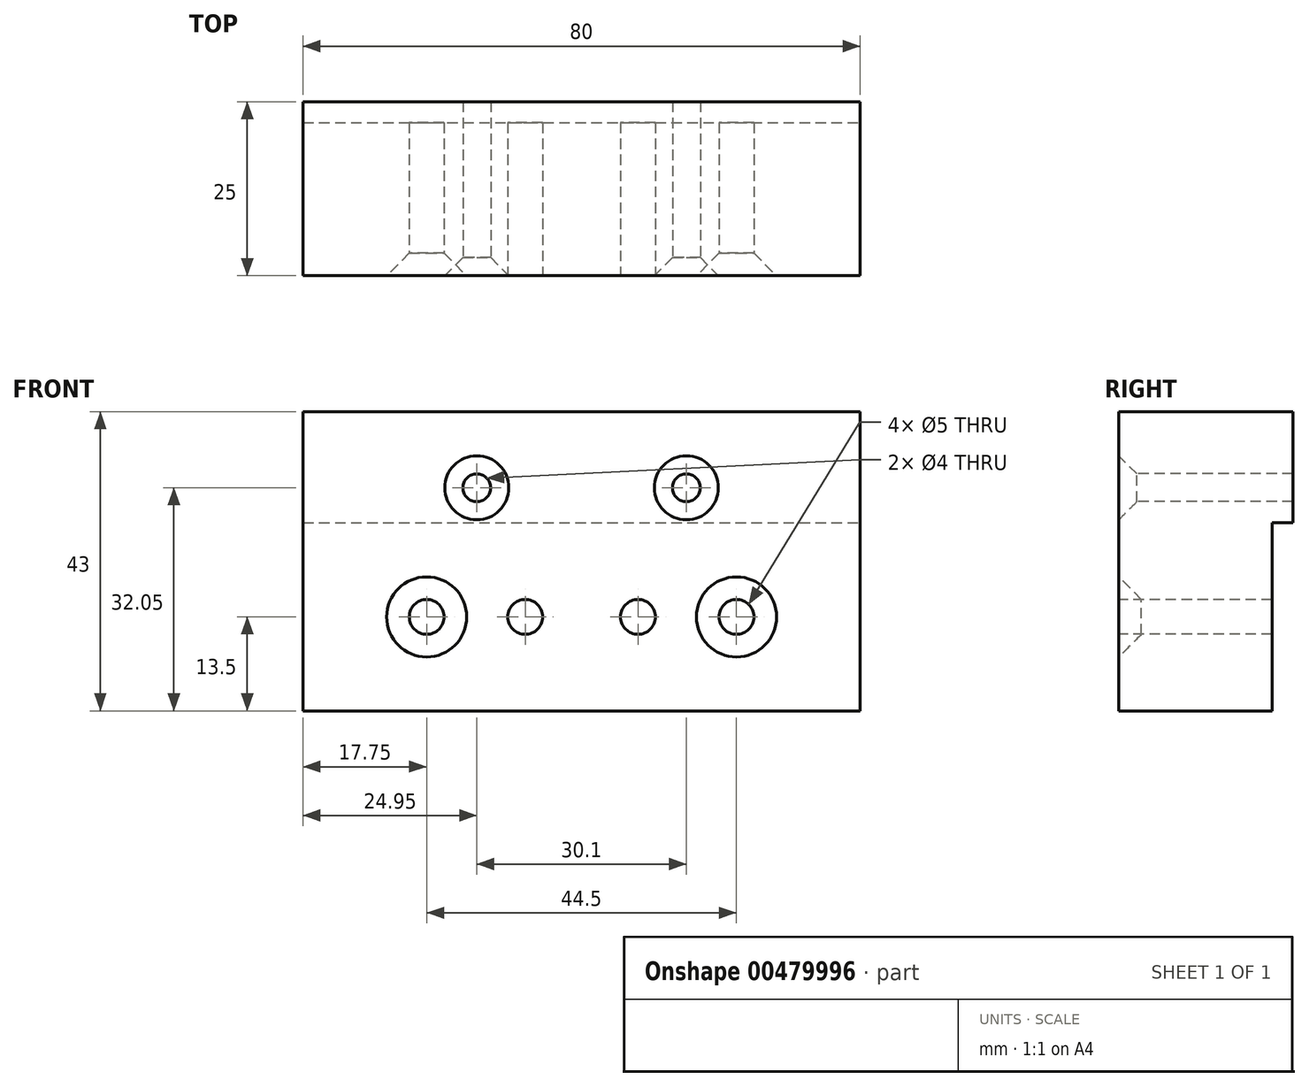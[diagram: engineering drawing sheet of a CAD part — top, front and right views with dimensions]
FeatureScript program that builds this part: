
annotation { "Feature Type Name" : "Feature", "Feature Type Description" : "" }
export const myFeature = defineFeature(function(context is Context, id is Id, definition is map)
    precondition{}
    {
        {
            var Q0;
            Q0=qCreatedBy(makeId("Front.planeOp"),FACE);
            var sketch = newSketch(context, id + "F0", { "sketchPlane" : qUnion([Q0])});
            skLineSegment(sketch, "E0.bottom", {"start": v(40, -21.5) * mm, "end": v(-40, -21.5) * mm});
            skLineSegment(sketch, "E0.top", {"start": v(40, 21.5) * mm, "end": v(-40, 21.5) * mm});
            skLineSegment(sketch, "E0.left", {"start": v(40, -21.5) * mm, "end": v(40, 21.5) * mm});
            skLineSegment(sketch, "E0.right", {"start": v(-40, -21.5) * mm, "end": v(-40, 21.5) * mm});
            skPoint(sketch, "E0.middle", {"position": v(0, 0) * mm});
            skSolve(sketch);
        }
        {
            var Q0;
            Q0=makeQuery(id+"F0.imprint","IMPRINT",FACE,{"disambiguationData":[TD([[makeQuery(id+"F0.imprint","IMPRINT",EDGE,{"derivedFrom":sQuery(id+"F0.wireOp",EDGE,"E0.bottom")}),-1.0]])]});
            extrude(context, id + "F1", {"entities" : qUnion([Q0]), "endBound" : BoundingType.SYMMETRIC, "depth" : 25 * mm});
        }
        {
            var Q0;
            Q0=makeQuery(id+"F1.opExtrude","SWEPT_FACE",FACE,{"disambiguationData":[OSD([sQuery(id+"F0.wireOp",EDGE,"E0.left")])]});
            var sketch = newSketch(context, id + "F2", { "sketchPlane" : qUnion([Q0])});
            skPoint(sketch, "E1.endSnap0", {"position": v(12.5, 0) * mm});
            skLineSegment(sketch, "E2", {"start": v(12.5, 5.5) * mm, "end": v(9.5, 5.5) * mm});
            skLineSegment(sketch, "E3", {"start": v(9.5, 5.5) * mm, "end": v(9.5, -21.5) * mm});
            skLineSegment(sketch, "E4", {"start": v(9.5, -21.5) * mm, "end": v(12.5, -21.5) * mm});
            skLineSegment(sketch, "E5", {"start": v(12.5, -21.5) * mm, "end": v(12.5, 5.5) * mm});
            skSolve(sketch);
        }
        {
            var Q0;
            Q0=makeQuery(id+"F2.imprint","IMPRINT",FACE,{"disambiguationData":[TD([[makeQuery(id+"F2.imprint","IMPRINT",EDGE,{"derivedFrom":sQuery(id+"F2.wireOp",EDGE,"E2")}),1.0]])]});
            extrude(context, id + "F3", {"entities" : qUnion([Q0]), "operationType" : NewBodyOperationType.REMOVE, "endBound" : BoundingType.THROUGH_ALL, "oppositeDirection" : true, "depth" : 25 * mm});
        }
        {
            var Q0;
            Q0=makeQuery(id+"F1.opExtrude","CAP_FACE",FACE,{"disambiguationData":[OSD([sQuery(id+"F0.wireOp",EDGE,"E0.bottom"),sQuery(id+"F0.wireOp",EDGE,"E0.top"),sQuery(id+"F0.wireOp",EDGE,"E0.left"),sQuery(id+"F0.wireOp",EDGE,"E0.right")])],"isStart":false});
            var sketch = newSketch(context, id + "F4", { "sketchPlane" : qUnion([Q0])});
            skPoint(sketch, "E6", {"position": v(-15.05, 10.55) * mm});
            skPoint(sketch, "E7", {"position": v(15.05, 10.55) * mm});
            skSolve(sketch);
        }
        {
            var Q0;
            Q0=sQuery(id+"F4.wireOp",VERTEX,"E6");
            var Q1;
            Q1=sQuery(id+"F4.wireOp",VERTEX,"E7");
            var Q2;
            Q2=makeQuery(id+"F1.opExtrude","SWEPT_BODY",BODY,{"disambiguationData":[OSD([sQuery(id+"F0.wireOp",EDGE,"E0.bottom"),sQuery(id+"F0.wireOp",EDGE,"E0.top"),sQuery(id+"F0.wireOp",EDGE,"E0.left"),sQuery(id+"F0.wireOp",EDGE,"E0.right")])]});
            hole(context, id + "F5", {"style" : HoleStyle.C_SINK, "endStyle" : HoleEndStyle.THROUGH, "standardTappedOrClearance" : lookupTablePath({ "standard" : "ISO", "size" : "4", "type" : "Drilled" }), "standardBlindInLast" : lookupTablePath({ "standard" : "ISO", "size" : "4", "type" : "Drilled" }), "holeDiameter" : 4 * mm, "cSinkDiameter" : 9.2 * mm, "cSinkAngle" : 90 * degree, "isTappedThrough" : true, "tappedDepth" : 12 * mm, "tapClearance" : 3, "locations" : qUnion([Q0, Q1]), "scope" : qUnion([Q2])});
        }
        {
            var Q0;
            Q0=makeQuery(id+"F1.opExtrude","CAP_FACE",FACE,{"disambiguationData":[OSD([sQuery(id+"F0.wireOp",EDGE,"E0.bottom"),sQuery(id+"F0.wireOp",EDGE,"E0.top"),sQuery(id+"F0.wireOp",EDGE,"E0.left"),sQuery(id+"F0.wireOp",EDGE,"E0.right")])],"isStart":false});
            var sketch = newSketch(context, id + "F6", { "sketchPlane" : qUnion([Q0])});
            skPoint(sketch, "E8", {"position": v(-22.25, -8) * mm});
            skPoint(sketch, "E9", {"position": v(-8.1, -8) * mm});
            skPoint(sketch, "E10", {"position": v(8.1, -8) * mm});
            skPoint(sketch, "E11", {"position": v(22.25, -8) * mm});
            skCircle(sketch, "E12", {"center": v(-8.1, -8) * mm, "radius": 2.5 * mm});
            skCircle(sketch, "E13", {"center": v(8.1, -8) * mm, "radius": 2.5 * mm});
            skSolve(sketch);
        }
        {
            var Q0;
            Q0=sQuery(id+"F6.wireOp",VERTEX,"E8");
            var Q1;
            Q1=sQuery(id+"F6.wireOp",VERTEX,"E11");
            var Q2;
            Q2=makeQuery(id+"F1.opExtrude","SWEPT_BODY",BODY,{"disambiguationData":[OSD([sQuery(id+"F0.wireOp",EDGE,"E0.bottom"),sQuery(id+"F0.wireOp",EDGE,"E0.top"),sQuery(id+"F0.wireOp",EDGE,"E0.left"),sQuery(id+"F0.wireOp",EDGE,"E0.right")])]});
            hole(context, id + "F7", {"style" : HoleStyle.C_SINK, "endStyle" : HoleEndStyle.THROUGH, "standardTappedOrClearance" : lookupTablePath({ "standard" : "ISO", "size" : "5", "type" : "Drilled" }), "standardBlindInLast" : lookupTablePath({ "standard" : "ISO", "size" : "5", "type" : "Drilled" }), "holeDiameter" : 5 * mm, "cSinkDiameter" : 11.5 * mm, "cSinkAngle" : 90 * degree, "isTappedThrough" : true, "tappedDepth" : 12 * mm, "tapClearance" : 3, "locations" : qUnion([Q0, Q1]), "scope" : qUnion([Q2])});
        }
        {
            var Q0;
            Q0=makeQuery(id+"F6.imprint","IMPRINT",FACE,{"disambiguationData":[TD([[makeQuery(id+"F6.imprint","IMPRINT",EDGE,{"derivedFrom":sQuery(id+"F6.wireOp",EDGE,"E12")}),1.0]])]});
            var Q1;
            Q1=makeQuery(id+"F6.imprint","IMPRINT",FACE,{"disambiguationData":[TD([[makeQuery(id+"F6.imprint","IMPRINT",EDGE,{"derivedFrom":sQuery(id+"F6.wireOp",EDGE,"E13")}),1.0]])]});
            extrude(context, id + "F8", {"entities" : qUnion([Q0, Q1]), "operationType" : NewBodyOperationType.REMOVE, "endBound" : BoundingType.THROUGH_ALL, "oppositeDirection" : true, "depth" : 25 * mm});
        }
    });
